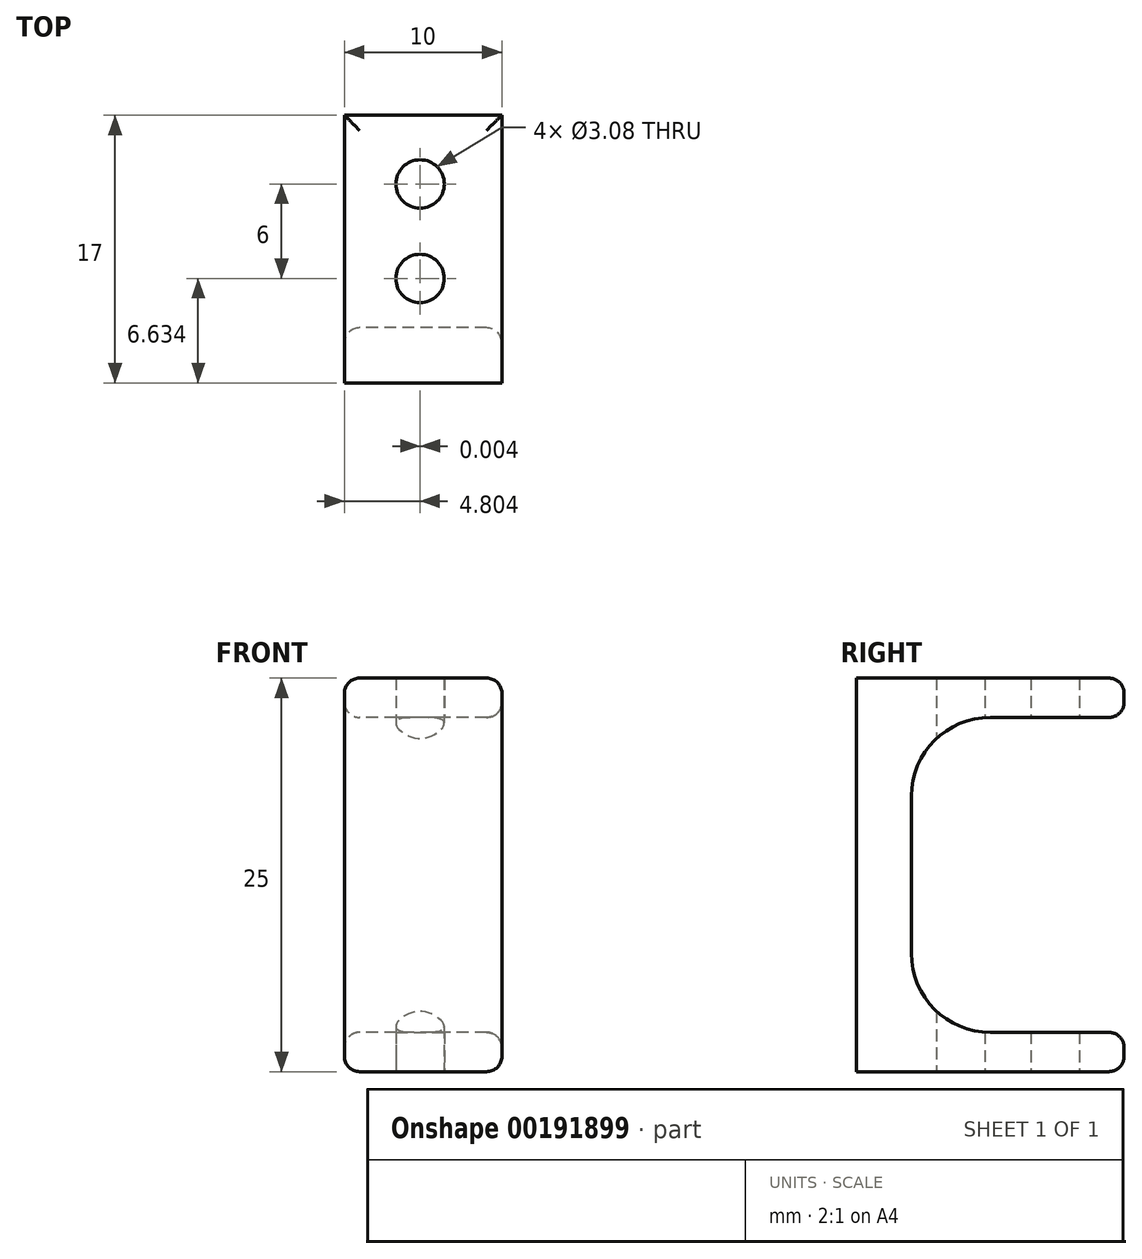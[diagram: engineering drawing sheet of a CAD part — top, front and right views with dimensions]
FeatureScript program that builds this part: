
annotation { "Feature Type Name" : "Feature", "Feature Type Description" : "" }
export const myFeature = defineFeature(function(context is Context, id is Id, definition is map)
    precondition{}
    {
        {
            var Q0;
            Q0=qCreatedBy(makeId("Right.planeOp"),FACE);
            var sketch = newSketch(context, id + "F0", { "sketchPlane" : qUnion([Q0])});
            skLineSegment(sketch, "E0", {"start": v(0, 0) * mm, "end": v(0, -25) * mm});
            skLineSegment(sketch, "E1", {"start": v(17, -25) * mm, "end": v(17, -22.5) * mm});
            skLineSegment(sketch, "E2", {"start": v(17, -22.5) * mm, "end": v(3.5, -22.5) * mm});
            skLineSegment(sketch, "E3", {"start": v(3.5, -22.5) * mm, "end": v(3.5, -2.5) * mm});
            skLineSegment(sketch, "E4", {"start": v(3.5, -2.5) * mm, "end": v(17, -2.5) * mm});
            skLineSegment(sketch, "E5", {"start": v(17, -2.5) * mm, "end": v(17, 0) * mm});
            skLineSegment(sketch, "E6", {"start": v(17, 0) * mm, "end": v(0, 0) * mm});
            skLineSegment(sketch, "E7", {"start": v(0, -25) * mm, "end": v(17, -25) * mm});
            skSolve(sketch);
        }
        {
            var Q0;
            Q0=makeQuery(id+"F0.imprint","IMPRINT",FACE,{"disambiguationData":[TD([[makeQuery(id+"F0.imprint","IMPRINT",EDGE,{"derivedFrom":sQuery(id+"F0.wireOp",EDGE,"E0")}),1.0]])]});
            extrude(context, id + "F1", {"entities" : qUnion([Q0]), "depth" : 10 * mm});
        }
        {
            var Q0;
            Q0=makeQuery(id+"F1.opExtrude","SWEPT_FACE",FACE,{"disambiguationData":[OSD([sQuery(id+"F0.wireOp",EDGE,"E7")])]});
            var sketch = newSketch(context, id + "F2", { "sketchPlane" : qUnion([Q0])});
            skCircle(sketch, "E8", {"center": v(4.8, -6.63) * mm, "radius": 1.54 * mm});
            skCircle(sketch, "E9.1.0.0", {"center": v(4.8, -12.63) * mm, "radius": 1.54 * mm});
            skLineSegment(sketch, "E9.direction1", {"start": v(4.8, -6.63) * mm, "end": v(4.8, -12.63) * mm, "construction": true});
            skSolve(sketch);
        }
        {
            var Q0;
            Q0=makeQuery(id+"F2.imprint","IMPRINT",FACE,{"disambiguationData":[TD([[makeQuery(id+"F2.imprint","IMPRINT",EDGE,{"derivedFrom":sQuery(id+"F2.wireOp",EDGE,"E8")}),1.0]])]});
            var Q1;
            Q1=makeQuery(id+"F2.imprint","IMPRINT",FACE,{"disambiguationData":[TD([[makeQuery(id+"F2.imprint","IMPRINT",EDGE,{"derivedFrom":sQuery(id+"F2.wireOp",EDGE,"E9.1.0.0")}),1.0]])]});
            extrude(context, id + "F3", {"entities" : qUnion([Q0, Q1]), "operationType" : NewBodyOperationType.REMOVE, "oppositeDirection" : true, "depth" : 25 * mm});
        }
        {
            var Q0;
            Q0=makeQuery(id+"F1.opExtrude","SWEPT_EDGE",EDGE,{"disambiguationData":[OSD([sQuery(id+"F0.wireOp",EDGE,"E3"),sQuery(id+"F0.wireOp",EDGE,"E4")])]});
            var Q1;
            Q1=makeQuery(id+"F1.opExtrude","SWEPT_EDGE",EDGE,{"disambiguationData":[OSD([sQuery(id+"F0.wireOp",EDGE,"E2"),sQuery(id+"F0.wireOp",EDGE,"E3")])]});
            fillet(context, id + "F4", {"entities" : qUnion([Q0, Q1]), "radius" : 5 * mm, "tangentPropagation" : true, "allowEdgeOverflow" : false});
        }
        {
            var Q0;
            Q0=makeQuery(id+"F1.opExtrude","SWEPT_EDGE",EDGE,{"disambiguationData":[OSD([sQuery(id+"F0.wireOp",EDGE,"E1"),sQuery(id+"F0.wireOp",EDGE,"E2")])]});
            var Q1;
            Q1=makeQuery(id+"F1.opExtrude","SWEPT_EDGE",EDGE,{"disambiguationData":[OSD([sQuery(id+"F0.wireOp",EDGE,"E1"),sQuery(id+"F0.wireOp",EDGE,"E7")])]});
            var Q2;
            Q2=makeQuery(id+"F1.opExtrude","SWEPT_EDGE",EDGE,{"disambiguationData":[OSD([sQuery(id+"F0.wireOp",EDGE,"E5"),sQuery(id+"F0.wireOp",EDGE,"E6")])]});
            var Q3;
            Q3=makeQuery(id+"F1.opExtrude","SWEPT_EDGE",EDGE,{"disambiguationData":[OSD([sQuery(id+"F0.wireOp",EDGE,"E4"),sQuery(id+"F0.wireOp",EDGE,"E5")])]});
            var Q4;
            Q4=makeQuery(id+"F1.opExtrude","CAP_EDGE",EDGE,{"disambiguationData":[OSD([sQuery(id+"F0.wireOp",EDGE,"E6")])],"isStart":true});
            var Q5;
            Q5=makeQuery(id+"F1.opExtrude","CAP_EDGE",EDGE,{"disambiguationData":[OSD([sQuery(id+"F0.wireOp",EDGE,"E6")])],"isStart":false});
            var Q6;
            Q6=makeQuery(id+"F1.opExtrude","CAP_EDGE",EDGE,{"disambiguationData":[OSD([sQuery(id+"F0.wireOp",EDGE,"E7")])],"isStart":false});
            var Q7;
            Q7=makeQuery(id+"F1.opExtrude","CAP_EDGE",EDGE,{"disambiguationData":[OSD([sQuery(id+"F0.wireOp",EDGE,"E7")])],"isStart":true});
            var Q8;
            {var subQ0=sQuery(id+"F0.wireOp",EDGE,"E4");var subQ1=sQuery(id+"F0.wireOp",EDGE,"E3");Q8=makeQuery(id+"F4.opFillet","BLEND_EDGE",EDGE,{"blendedFrom":[makeQuery(id+"F1.opExtrude","SWEPT_EDGE",EDGE,{"disambiguationData":[OSD([subQ1,subQ0])]}),makeQuery(id+"F1.opExtrude","CAP_FACE",FACE,{"disambiguationData":[OSD([sQuery(id+"F0.wireOp",EDGE,"E0"),sQuery(id+"F0.wireOp",EDGE,"E1"),sQuery(id+"F0.wireOp",EDGE,"E2"),subQ1,subQ0,sQuery(id+"F0.wireOp",EDGE,"E5"),sQuery(id+"F0.wireOp",EDGE,"E6"),sQuery(id+"F0.wireOp",EDGE,"E7")])],"isStart":false})],"blendedInto":[makeQuery(id+"F1.opExtrude","CAP_FACE",FACE,{"disambiguationData":[OSD([sQuery(id+"F0.wireOp",EDGE,"E0"),sQuery(id+"F0.wireOp",EDGE,"E1"),sQuery(id+"F0.wireOp",EDGE,"E2"),subQ1,subQ0,sQuery(id+"F0.wireOp",EDGE,"E5"),sQuery(id+"F0.wireOp",EDGE,"E6"),sQuery(id+"F0.wireOp",EDGE,"E7")])],"isStart":false})]});}
            var Q9;
            {var subQ0=sQuery(id+"F0.wireOp",EDGE,"E4");var subQ1=sQuery(id+"F0.wireOp",EDGE,"E3");Q9=makeQuery(id+"F4.opFillet","BLEND_EDGE",EDGE,{"blendedFrom":[makeQuery(id+"F1.opExtrude","SWEPT_EDGE",EDGE,{"disambiguationData":[OSD([subQ1,subQ0])]}),makeQuery(id+"F1.opExtrude","CAP_FACE",FACE,{"disambiguationData":[OSD([sQuery(id+"F0.wireOp",EDGE,"E0"),sQuery(id+"F0.wireOp",EDGE,"E1"),sQuery(id+"F0.wireOp",EDGE,"E2"),subQ1,subQ0,sQuery(id+"F0.wireOp",EDGE,"E5"),sQuery(id+"F0.wireOp",EDGE,"E6"),sQuery(id+"F0.wireOp",EDGE,"E7")])],"isStart":true})],"blendedInto":[makeQuery(id+"F1.opExtrude","CAP_FACE",FACE,{"disambiguationData":[OSD([sQuery(id+"F0.wireOp",EDGE,"E0"),sQuery(id+"F0.wireOp",EDGE,"E1"),sQuery(id+"F0.wireOp",EDGE,"E2"),subQ1,subQ0,sQuery(id+"F0.wireOp",EDGE,"E5"),sQuery(id+"F0.wireOp",EDGE,"E6"),sQuery(id+"F0.wireOp",EDGE,"E7")])],"isStart":true})]});}
            var Q10;
            Q10=makeQuery(id+"F1.opExtrude","CAP_EDGE",EDGE,{"disambiguationData":[OSD([sQuery(id+"F0.wireOp",EDGE,"E3")])],"isStart":true});
            fillet(context, id + "F5", {"entities" : qUnion([Q0, Q1, Q2, Q3, Q4, Q5, Q6, Q7, Q8, Q9, Q10]), "radius" : 0.97 * mm, "tangentPropagation" : true, "allowEdgeOverflow" : false});
        }
    });
